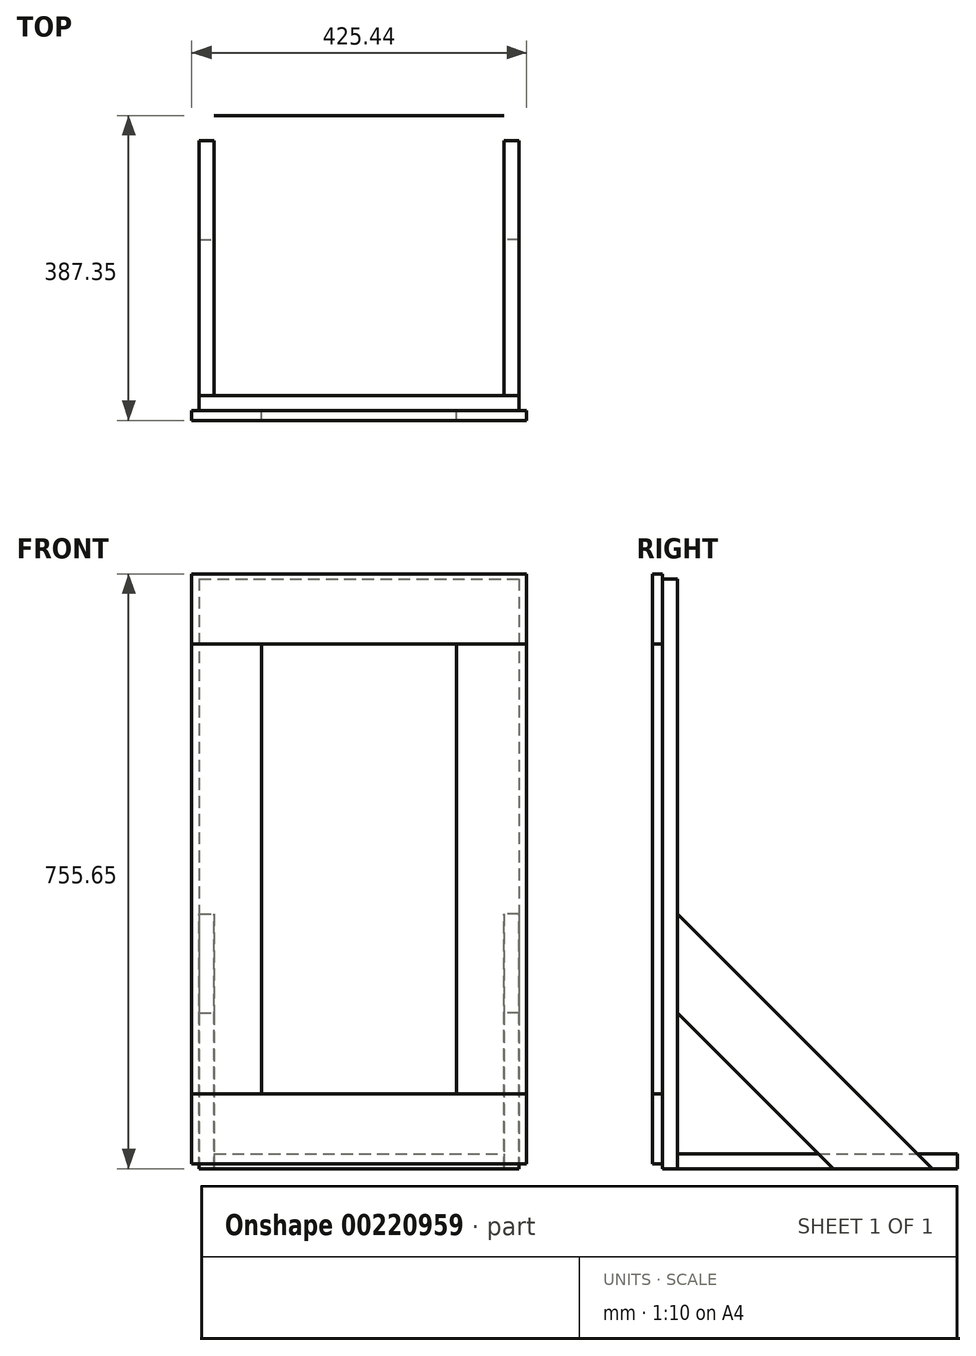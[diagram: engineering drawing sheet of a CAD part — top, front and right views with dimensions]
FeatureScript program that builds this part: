
annotation { "Feature Type Name" : "Feature", "Feature Type Description" : "" }
export const myFeature = defineFeature(function(context is Context, id is Id, definition is map)
    precondition{}
    {
        {
            var Q0;
            Q0=qCreatedBy(makeId("Front.planeOp"),FACE);
            var sketch = newSketch(context, id + "F0", { "sketchPlane" : qUnion([Q0])});
            skLineSegment(sketch, "E0.bottom", {"start": v(-203.2, 374.65) * mm, "end": v(203.2, 374.65) * mm});
            skLineSegment(sketch, "E0.top", {"start": v(-203.2, -374.65) * mm, "end": v(203.2, -374.65) * mm});
            skLineSegment(sketch, "E0.left", {"start": v(-203.2, 374.65) * mm, "end": v(-203.2, -374.65) * mm});
            skLineSegment(sketch, "E0.right", {"start": v(203.2, 374.65) * mm, "end": v(203.2, -374.65) * mm});
            skPoint(sketch, "E0.middle", {"position": v(0, 0) * mm});
            skSolve(sketch);
        }
        {
            var Q0;
            Q0 = qSketchRegion(id + "F0", true);
            extrude(context, id + "F1", {"entities" : qUnion([Q0]), "depth" : 19.05 * mm});
        }
        {
            var Q0;
            Q0=makeQuery(id+"F1.opExtrude","SWEPT_FACE",FACE,{"disambiguationData":[OSD([sQuery(id+"F0.wireOp",EDGE,"E0.top")])]});
            var sketch = newSketch(context, id + "F2", { "sketchPlane" : qUnion([Q0])});
            skLineSegment(sketch, "E1.bottom", {"start": v(-184.15, 0) * mm, "end": v(184.15, 0) * mm});
            skLineSegment(sketch, "E1.top", {"start": v(-184.15, -355.6) * mm, "end": v(184.15, -355.6) * mm});
            skLineSegment(sketch, "E1.left", {"start": v(-184.15, 0) * mm, "end": v(-184.15, -355.6) * mm});
            skLineSegment(sketch, "E1.right", {"start": v(184.15, 0) * mm, "end": v(184.15, -355.6) * mm});
            skLineSegment(sketch, "E2", {"start": v(0, 0) * mm, "end": v(0, -355.6) * mm, "construction": true});
            skSolve(sketch);
        }
        {
            var Q0;
            Q0 = qSketchRegion(id + "F2", true);
            extrude(context, id + "F3", {"entities" : qUnion([Q0]), "oppositeDirection" : true, "depth" : 19.05 * mm});
        }
        {
            var Q0;
            Q0=makeQuery(id+"F3.opExtrude","SWEPT_FACE",FACE,{"disambiguationData":[OSD([sQuery(id+"F2.wireOp",EDGE,"E1.left")])]});
            var sketch = newSketch(context, id + "F4", { "sketchPlane" : qUnion([Q0])});
            skLineSegment(sketch, "E3", {"start": v(-323.29, -374.65) * mm, "end": v(0, -51.36) * mm});
            skLineSegment(sketch, "E4", {"start": v(0, -51.36) * mm, "end": v(0, -177.08) * mm});
            skLineSegment(sketch, "E5", {"start": v(0, -177.08) * mm, "end": v(-197.57, -374.65) * mm});
            skLineSegment(sketch, "E6", {"start": v(-197.57, -374.65) * mm, "end": v(-323.29, -374.65) * mm});
            skSolve(sketch);
        }
        {
            var Q0;
            Q0 = qSketchRegion(id + "F4", true);
            extrude(context, id + "F5", {"entities" : qUnion([Q0]), "depth" : 19.05 * mm});
        }
        {
            var Q0;
            Q0=makeQuery(id+"F5.opExtrude","SWEPT_BODY",BODY,{"disambiguationData":[OSD([sQuery(id+"F4.wireOp",EDGE,"E3"),sQuery(id+"F4.wireOp",EDGE,"E4"),sQuery(id+"F4.wireOp",EDGE,"E5"),sQuery(id+"F4.wireOp",EDGE,"E6")])]});
            var Q1;
            Q1=qCreatedBy(makeId("Right.planeOp"),FACE);
            mirror(context, id + "F6", {"entities" : qUnion([Q0]), "mirrorPlane" : qUnion([Q1])});
        }
        {
            var Q0;
            Q0=makeQuery(id+"F1.opExtrude","CAP_FACE",FACE,{"disambiguationData":[OSD([sQuery(id+"F0.wireOp",EDGE,"E0.bottom"),sQuery(id+"F0.wireOp",EDGE,"E0.top"),sQuery(id+"F0.wireOp",EDGE,"E0.left"),sQuery(id+"F0.wireOp",EDGE,"E0.right")])],"isStart":false});
            var sketch = newSketch(context, id + "F7", { "sketchPlane" : qUnion([Q0])});
            skLineSegment(sketch, "E7.bottom", {"start": v(-212.73, 381) * mm, "end": v(212.72, 381) * mm});
            skLineSegment(sketch, "E7.top", {"start": v(-212.73, -368.3) * mm, "end": v(212.73, -368.3) * mm});
            skLineSegment(sketch, "E7.left", {"start": v(-212.73, 381) * mm, "end": v(-212.73, -368.3) * mm});
            skLineSegment(sketch, "E7.right", {"start": v(212.72, 381) * mm, "end": v(212.73, -368.3) * mm});
            skLineSegment(sketch, "E8.bottom", {"start": v(-212.73, 292.1) * mm, "end": v(212.73, 292.1) * mm});
            skLineSegment(sketch, "E8.top", {"start": v(-212.73, -279.4) * mm, "end": v(212.73, -279.4) * mm});
            skLineSegment(sketch, "E9", {"start": v(-123.83, 292.1) * mm, "end": v(-123.83, -279.4) * mm});
            skLineSegment(sketch, "E10", {"start": v(123.83, 292.1) * mm, "end": v(123.83, -279.4) * mm});
            skSolve(sketch);
        }
        {
            var Q0;
            {var subQ0=makeQuery(id+"F1.opExtrude","CAP_EDGE",EDGE,{"disambiguationData":[OSD([sQuery(id+"F0.wireOp",EDGE,"E0.bottom")])],"isStart":false});Q0=makeQuery(id+"F7.imprint","IMPRINT",FACE,{"disambiguationData":[TD([[makeQuery(id+"F7.imprint","IMPRINT",EDGE,{"derivedFrom":subQ0}),-1.0]])]});}
            var Q1;
            {var subQ7=sQuery(id+"F7.wireOp",EDGE,"E7.bottom");Q1=makeQuery(id+"F7.imprint","IMPRINT",FACE,{"disambiguationData":[TD([[makeQuery(id+"F7.imprint","IMPRINT",EDGE,{"derivedFrom":subQ7}),-1.0]])]});}
            var Q2;
            {var subQ5=makeQuery(id+"F1.opExtrude","CAP_EDGE",EDGE,{"disambiguationData":[OSD([sQuery(id+"F0.wireOp",EDGE,"E0.left")])],"isStart":false});var subQ7=sQuery(id+"F7.wireOp",EDGE,"E7.top");var subQ9=makeQuery(id+"F7.imprint","INTERSECT",VERTEX,{"derivedFrom":[subQ5,subQ7]});Q2=makeQuery(id+"F7.imprint","IMPRINT",FACE,{"disambiguationData":[TD([[makeQuery(id+"F7.imprint","IMPRINT",EDGE,{"disambiguationData":[TD([[subQ9,-1.0]])],"derivedFrom":subQ7}),1.0]])]});}
            var Q3;
            {var subQ0=sQuery(id+"F7.wireOp",EDGE,"E7.left");var subQ1=sQuery(id+"F7.wireOp",EDGE,"E7.top");var subQ2=makeQuery(id+"F7.imprint","INTERSECT",VERTEX,{"derivedFrom":[subQ1,subQ0]});Q3=makeQuery(id+"F7.imprint","IMPRINT",FACE,{"disambiguationData":[TD([[makeQuery(id+"F7.imprint","IMPRINT",EDGE,{"disambiguationData":[TD([[subQ2,-1.0]])],"derivedFrom":subQ1}),1.0]])]});}
            var Q4;
            {var subQ0=sQuery(id+"F7.wireOp",EDGE,"E7.right");var subQ1=sQuery(id+"F7.wireOp",EDGE,"E7.top");var subQ2=makeQuery(id+"F7.imprint","INTERSECT",VERTEX,{"derivedFrom":[subQ1,subQ0]});Q4=makeQuery(id+"F7.imprint","IMPRINT",FACE,{"disambiguationData":[TD([[makeQuery(id+"F7.imprint","IMPRINT",EDGE,{"disambiguationData":[TD([[subQ2,1.0]])],"derivedFrom":subQ1}),1.0]])]});}
            extrude(context, id + "F8", {"entities" : qUnion([Q0, Q1, Q2, Q3, Q4]), "depth" : 12.7 * mm});
        }
        {
            var Q0;
            {var subQ0=sQuery(id+"F7.wireOp",EDGE,"E9");Q0=makeQuery(id+"F7.imprint","IMPRINT",FACE,{"disambiguationData":[TD([[makeQuery(id+"F7.imprint","IMPRINT",EDGE,{"derivedFrom":subQ0}),-1.0]])]});}
            var Q1;
            {var subQ0=sQuery(id+"F7.wireOp",EDGE,"E8.bottom");var subQ1=sQuery(id+"F7.wireOp",EDGE,"E7.left");var subQ2=makeQuery(id+"F7.imprint","INTERSECT",VERTEX,{"derivedFrom":[subQ1,subQ0]});Q1=makeQuery(id+"F7.imprint","IMPRINT",FACE,{"disambiguationData":[TD([[makeQuery(id+"F7.imprint","IMPRINT",EDGE,{"disambiguationData":[TD([[subQ2,-1.0]])],"derivedFrom":subQ1}),1.0]])]});}
            var Q2;
            {var subQ0=sQuery(id+"F7.wireOp",EDGE,"E10");Q2=makeQuery(id+"F7.imprint","IMPRINT",FACE,{"disambiguationData":[TD([[makeQuery(id+"F7.imprint","IMPRINT",EDGE,{"derivedFrom":subQ0}),1.0]])]});}
            var Q3;
            {var subQ0=sQuery(id+"F7.wireOp",EDGE,"E8.bottom");var subQ1=sQuery(id+"F7.wireOp",EDGE,"E7.right");var subQ2=makeQuery(id+"F7.imprint","INTERSECT",VERTEX,{"derivedFrom":[subQ1,subQ0]});Q3=makeQuery(id+"F7.imprint","IMPRINT",FACE,{"disambiguationData":[TD([[makeQuery(id+"F7.imprint","IMPRINT",EDGE,{"disambiguationData":[TD([[subQ2,-1.0]])],"derivedFrom":subQ1}),-1.0]])]});}
            extrude(context, id + "F9", {"entities" : qUnion([Q0, Q1, Q2, Q3]), "depth" : 12.7 * mm});
        }
    });
